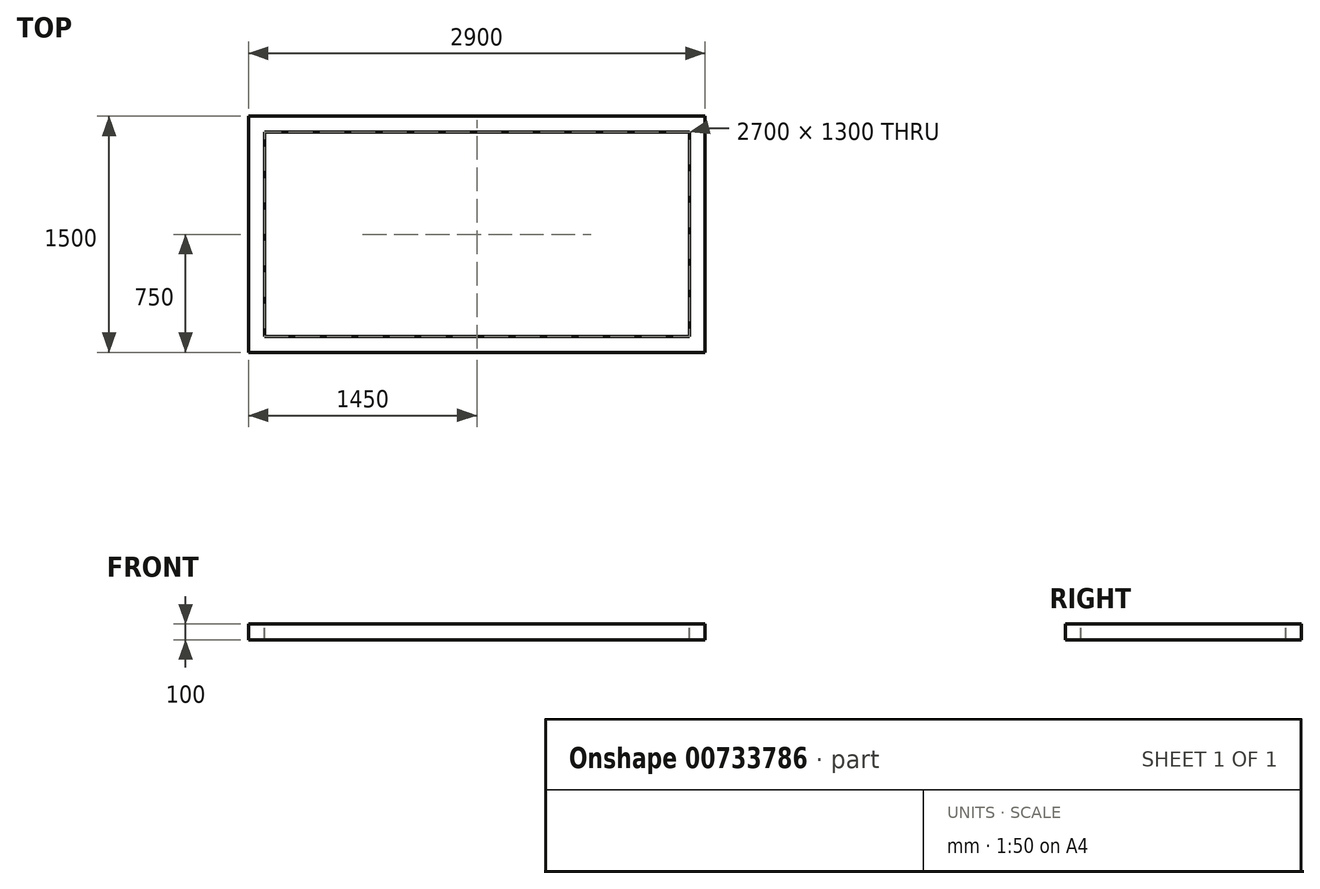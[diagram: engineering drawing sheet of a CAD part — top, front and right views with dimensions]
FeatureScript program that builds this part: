
annotation { "Feature Type Name" : "Feature", "Feature Type Description" : "" }
export const myFeature = defineFeature(function(context is Context, id is Id, definition is map)
    precondition{}
    {
        {
            var Q0;
            Q0=qCreatedBy(makeId("Top.planeOp"),FACE);
            var sketch = newSketch(context, id + "F0", { "sketchPlane" : qUnion([Q0])});
            skPoint(sketch, "E0.middle", {"position": v(0, 0) * mm});
            skLineSegment(sketch, "E1.bottom", {"start": v(-1450, -750) * mm, "end": v(1450, -750) * mm});
            skLineSegment(sketch, "E1.top", {"start": v(-1450, 750) * mm, "end": v(1450, 750) * mm});
            skLineSegment(sketch, "E1.left", {"start": v(-1450, -750) * mm, "end": v(-1450, 750) * mm});
            skLineSegment(sketch, "E1.right", {"start": v(1450, -750) * mm, "end": v(1450, 750) * mm});
            skPoint(sketch, "E2.endSnap0", {"position": v(-1450, 0) * mm});
            skLineSegment(sketch, "E3.0", {"start": v(-1350, -650) * mm, "end": v(-1350, 650) * mm});
            skLineSegment(sketch, "E3.1", {"start": v(-1350, -650) * mm, "end": v(1350, -650) * mm});
            skLineSegment(sketch, "E3.2", {"start": v(1350, -650) * mm, "end": v(1350, 650) * mm});
            skLineSegment(sketch, "E3.3", {"start": v(-1350, 650) * mm, "end": v(1350, 650) * mm});
            skSolve(sketch);
        }
        {
            var Q0;
            Q0=makeQuery(id+"F0.imprint","IMPRINT",FACE,{"disambiguationData":[TD([[makeQuery(id+"F0.imprint","IMPRINT",EDGE,{"derivedFrom":sQuery(id+"F0.wireOp",EDGE,"E1.bottom")}),1.0]])]});
            extrude(context, id + "F1", {"entities" : qUnion([Q0]), "oppositeDirection" : true, "depth" : 100 * mm, "offsetDistance" : 25 * mm});
        }
    });
